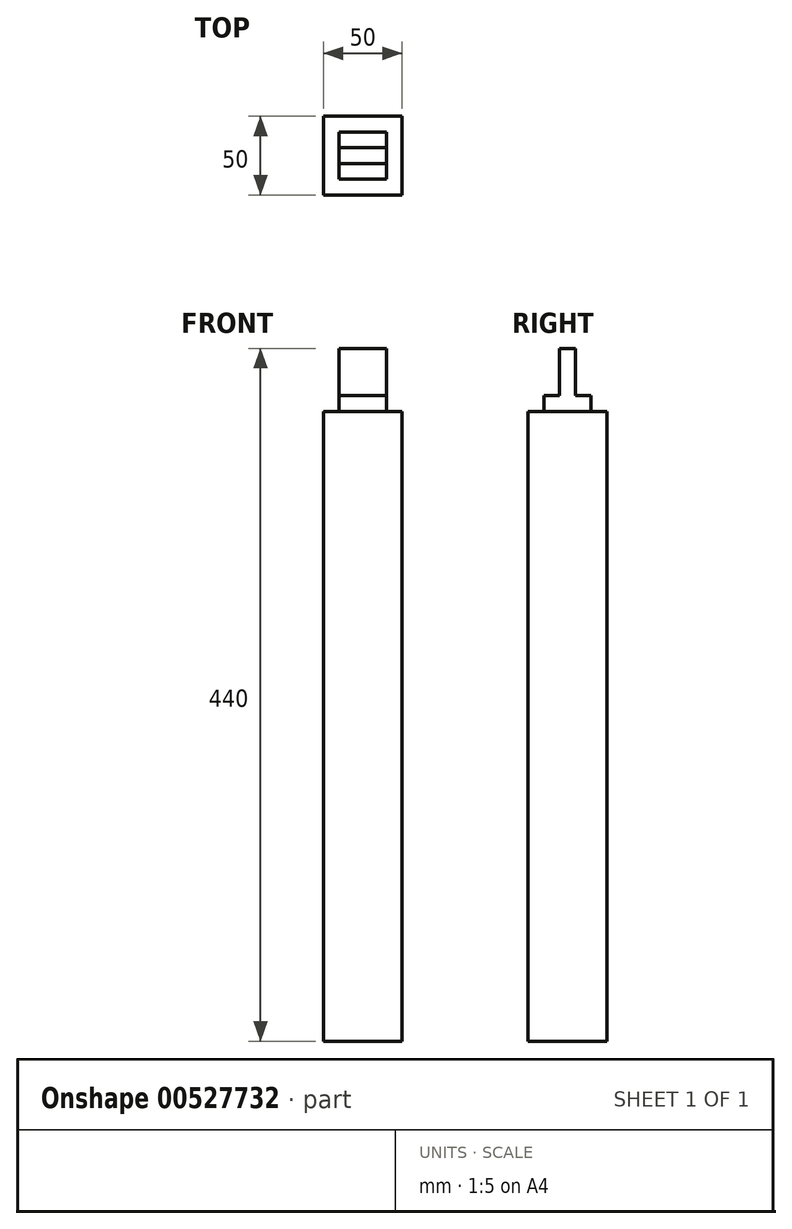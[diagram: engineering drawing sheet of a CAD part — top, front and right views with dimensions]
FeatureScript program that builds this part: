
annotation { "Feature Type Name" : "Feature", "Feature Type Description" : "" }
export const myFeature = defineFeature(function(context is Context, id is Id, definition is map)
    precondition{}
    {
        {
            var Q0;
            Q0=qCreatedBy(makeId("Top.planeOp"),FACE);
            var sketch = newSketch(context, id + "F0", { "sketchPlane" : qUnion([Q0])});
            skLineSegment(sketch, "E0.bottom", {"start": v(0, 0) * mm, "end": v(-50, 0) * mm});
            skLineSegment(sketch, "E0.top", {"start": v(0, -50) * mm, "end": v(-50, -50) * mm});
            skLineSegment(sketch, "E0.left", {"start": v(0, 0) * mm, "end": v(0, -50) * mm});
            skLineSegment(sketch, "E0.right", {"start": v(-50, 0) * mm, "end": v(-50, -50) * mm});
            skSolve(sketch);
        }
        {
            var Q0;
            Q0=makeQuery(id+"F0.imprint","IMPRINT",FACE,{"disambiguationData":[TD([[makeQuery(id+"F0.imprint","IMPRINT",EDGE,{"derivedFrom":sQuery(id+"F0.wireOp",EDGE,"E0.bottom")}),1.0]])]});
            extrude(context, id + "F1", {"entities" : qUnion([Q0]), "depth" : -400 * mm, "offsetDistance" : 25 * mm});
        }
        {
            var Q0;
            Q0=makeQuery(id+"F1.opExtrude","CAP_FACE",FACE,{"disambiguationData":[OSD([sQuery(id+"F0.wireOp",EDGE,"E0.bottom"),sQuery(id+"F0.wireOp",EDGE,"E0.top"),sQuery(id+"F0.wireOp",EDGE,"E0.left"),sQuery(id+"F0.wireOp",EDGE,"E0.right")])],"isStart":true});
            var sketch = newSketch(context, id + "F2", { "sketchPlane" : qUnion([Q0])});
            skLineSegment(sketch, "E1.bottom", {"start": v(-40, -10) * mm, "end": v(-10, -10) * mm});
            skLineSegment(sketch, "E1.top", {"start": v(-40, -40) * mm, "end": v(-10, -40) * mm});
            skLineSegment(sketch, "E1.left", {"start": v(-40, -10) * mm, "end": v(-40, -40) * mm});
            skLineSegment(sketch, "E1.right", {"start": v(-10, -10) * mm, "end": v(-10, -40) * mm});
            skSolve(sketch);
        }
        {
            var Q0;
            Q0 = qSketchRegion(id + "F2", true);
            extrude(context, id + "F3", {"entities" : qUnion([Q0]), "operationType" : NewBodyOperationType.ADD, "depth" : 40 * mm, "offsetDistance" : 25 * mm});
        }
        {
            var Q0;
            Q0=makeQuery(id+"F3.opExtrude","CAP_FACE",FACE,{"disambiguationData":[OSD([sQuery(id+"F2.wireOp",EDGE,"E1.bottom"),sQuery(id+"F2.wireOp",EDGE,"E1.top"),sQuery(id+"F2.wireOp",EDGE,"E1.left"),sQuery(id+"F2.wireOp",EDGE,"E1.right")])],"isStart":false});
            var sketch = newSketch(context, id + "F4", { "sketchPlane" : qUnion([Q0])});
            skLineSegment(sketch, "E2.bottom", {"start": v(-40, -40) * mm, "end": v(-10, -40) * mm});
            skLineSegment(sketch, "E2.top", {"start": v(-40, -30) * mm, "end": v(-10, -30) * mm});
            skLineSegment(sketch, "E2.left", {"start": v(-40, -40) * mm, "end": v(-40, -30) * mm});
            skLineSegment(sketch, "E2.right", {"start": v(-10, -40) * mm, "end": v(-10, -30) * mm});
            skLineSegment(sketch, "E3.bottom", {"start": v(-40, -10) * mm, "end": v(-10, -10) * mm});
            skLineSegment(sketch, "E3.top", {"start": v(-40, -20) * mm, "end": v(-10, -20) * mm});
            skLineSegment(sketch, "E3.left", {"start": v(-40, -10) * mm, "end": v(-40, -20) * mm});
            skLineSegment(sketch, "E3.right", {"start": v(-10, -10) * mm, "end": v(-10, -20) * mm});
            skSolve(sketch);
        }
        {
            var Q0;
            Q0=makeQuery(id+"F4.imprint","IMPRINT",FACE,{"disambiguationData":[TD([[makeQuery(id+"F4.imprint","IMPRINT",EDGE,{"derivedFrom":sQuery(id+"F4.wireOp",EDGE,"E2.bottom")}),1.0]])]});
            var Q1;
            Q1=makeQuery(id+"F4.imprint","IMPRINT",FACE,{"disambiguationData":[TD([[makeQuery(id+"F4.imprint","IMPRINT",EDGE,{"derivedFrom":sQuery(id+"F4.wireOp",EDGE,"E3.bottom")}),-1.0]])]});
            extrude(context, id + "F5", {"entities" : qUnion([Q0, Q1]), "operationType" : NewBodyOperationType.REMOVE, "oppositeDirection" : true, "depth" : 30 * mm, "offsetDistance" : 25 * mm});
        }
    });
